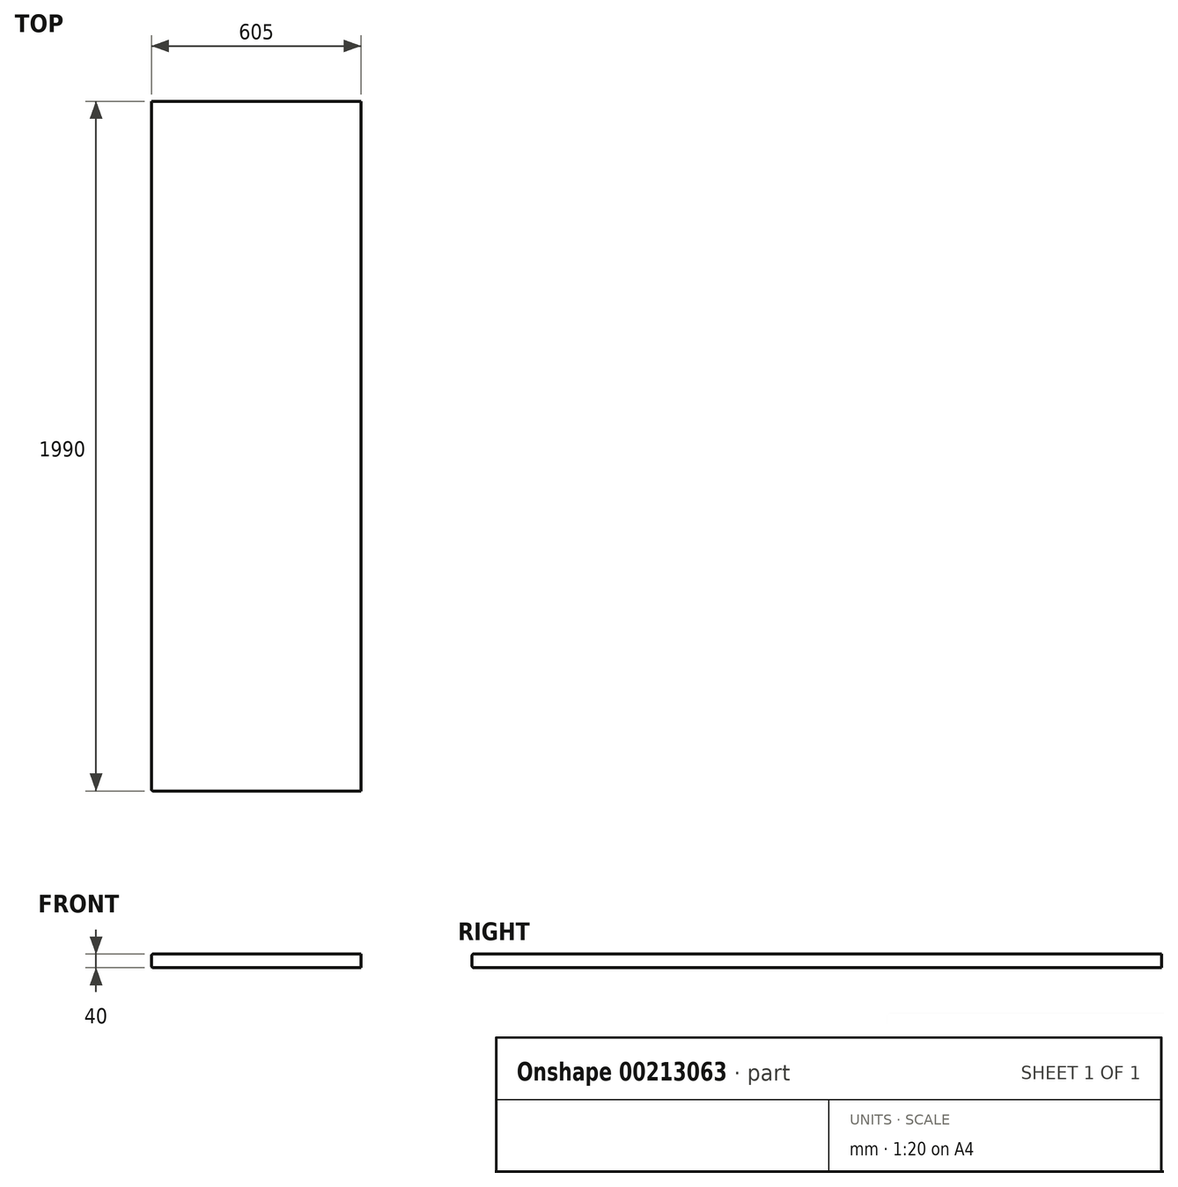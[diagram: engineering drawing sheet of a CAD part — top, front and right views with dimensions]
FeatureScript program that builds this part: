
annotation { "Feature Type Name" : "Feature", "Feature Type Description" : "" }
export const myFeature = defineFeature(function(context is Context, id is Id, definition is map)
    precondition{}
    {
        {
            var Q0;
            Q0=qCreatedBy(makeId("Top.planeOp"),FACE);
            var sketch = newSketch(context, id + "F0", { "sketchPlane" : qUnion([Q0])});
            skLineSegment(sketch, "E0.bottom", {"start": v(302.5, -995) * mm, "end": v(-302.5, -995) * mm});
            skLineSegment(sketch, "E0.top", {"start": v(302.5, 995) * mm, "end": v(-302.5, 995) * mm});
            skLineSegment(sketch, "E0.left", {"start": v(302.5, -995) * mm, "end": v(302.5, 995) * mm});
            skLineSegment(sketch, "E0.right", {"start": v(-302.5, -995) * mm, "end": v(-302.5, 995) * mm});
            skPoint(sketch, "E0.middle", {"position": v(0, 0) * mm});
            skPoint(sketch, "E1.visualSharp", {"position": v(-302.5, -995) * mm});
            skSolve(sketch);
        }
        {
            var Q0;
            Q0=makeQuery(id+"F0.imprint","IMPRINT",FACE,{"disambiguationData":[TD([[makeQuery(id+"F0.imprint","IMPRINT",EDGE,{"derivedFrom":sQuery(id+"F0.wireOp",EDGE,"E0.bottom")}),-1.0]])]});
            extrude(context, id + "F1", {"entities" : qUnion([Q0]), "endBound" : BoundingType.SYMMETRIC, "depth" : 40 * mm});
        }
        {
            var Q0;
            Q0=makeQuery(id+"F1.opExtrude","CAP_EDGE",EDGE,{"disambiguationData":[OSD([sQuery(id+"F0.wireOp",EDGE,"E0.right")])],"isStart":false});
            var Q1;
            Q1=makeQuery(id+"F1.opExtrude","SWEPT_EDGE",EDGE,{"disambiguationData":[OSD([sQuery(id+"F0.wireOp",EDGE,"E0.bottom"),sQuery(id+"F0.wireOp",EDGE,"E0.right")])]});
            var Q2;
            Q2=makeQuery(id+"F1.opExtrude","CAP_EDGE",EDGE,{"disambiguationData":[OSD([sQuery(id+"F0.wireOp",EDGE,"E0.bottom")])],"isStart":false});
            var Q3;
            Q3=makeQuery(id+"F1.opExtrude","CAP_EDGE",EDGE,{"disambiguationData":[OSD([sQuery(id+"F0.wireOp",EDGE,"E0.bottom")])],"isStart":true});
            var Q4;
            Q4=makeQuery(id+"F1.opExtrude","CAP_EDGE",EDGE,{"disambiguationData":[OSD([sQuery(id+"F0.wireOp",EDGE,"E0.right")])],"isStart":true});
            fillet(context, id + "F2", {"entities" : qUnion([Q0, Q1, Q2, Q3, Q4]), "radius" : 5 * mm, "tangentPropagation" : true, "allowEdgeOverflow" : false});
        }
    });
